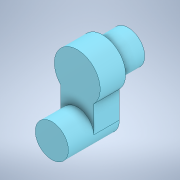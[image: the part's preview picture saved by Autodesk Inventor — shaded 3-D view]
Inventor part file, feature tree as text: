
AUTODESK INVENTOR PART (.ipt)
format: ipt  version: 2022 (Build 260153000, 153)  size: 139,264 bytes
history: native  units: in
note: dims shown in document units (in); Inventor stores cm internally (conversion verified against a paired STEP export)
features: extrude x3, sketch x2
ambient origin geometry x8: Origin, YZ Plane, XZ Plane, XY Plane, X Axis, Y Axis, Z Axis, Center Point
bodies: Solid1 (feature_tree)
feature tree (5):
  sketch  "Sketch2"  dims[d0=0.1969in d1=0.0in d2=0.1969in d3=0.0in]
  extrude  "Extrusion1"  Depth=0.1969in TaperAngle=0.0deg
  extrude  "Extrusion2"  Depth=0.1969in
  extrude  "Extrusion3"  Depth=0.1969in
  sketch  "Sketch3"  dims[d4=0.1969in d5=0.0in d6=0.2559in d7=0.3543in d8=0.3346in]
